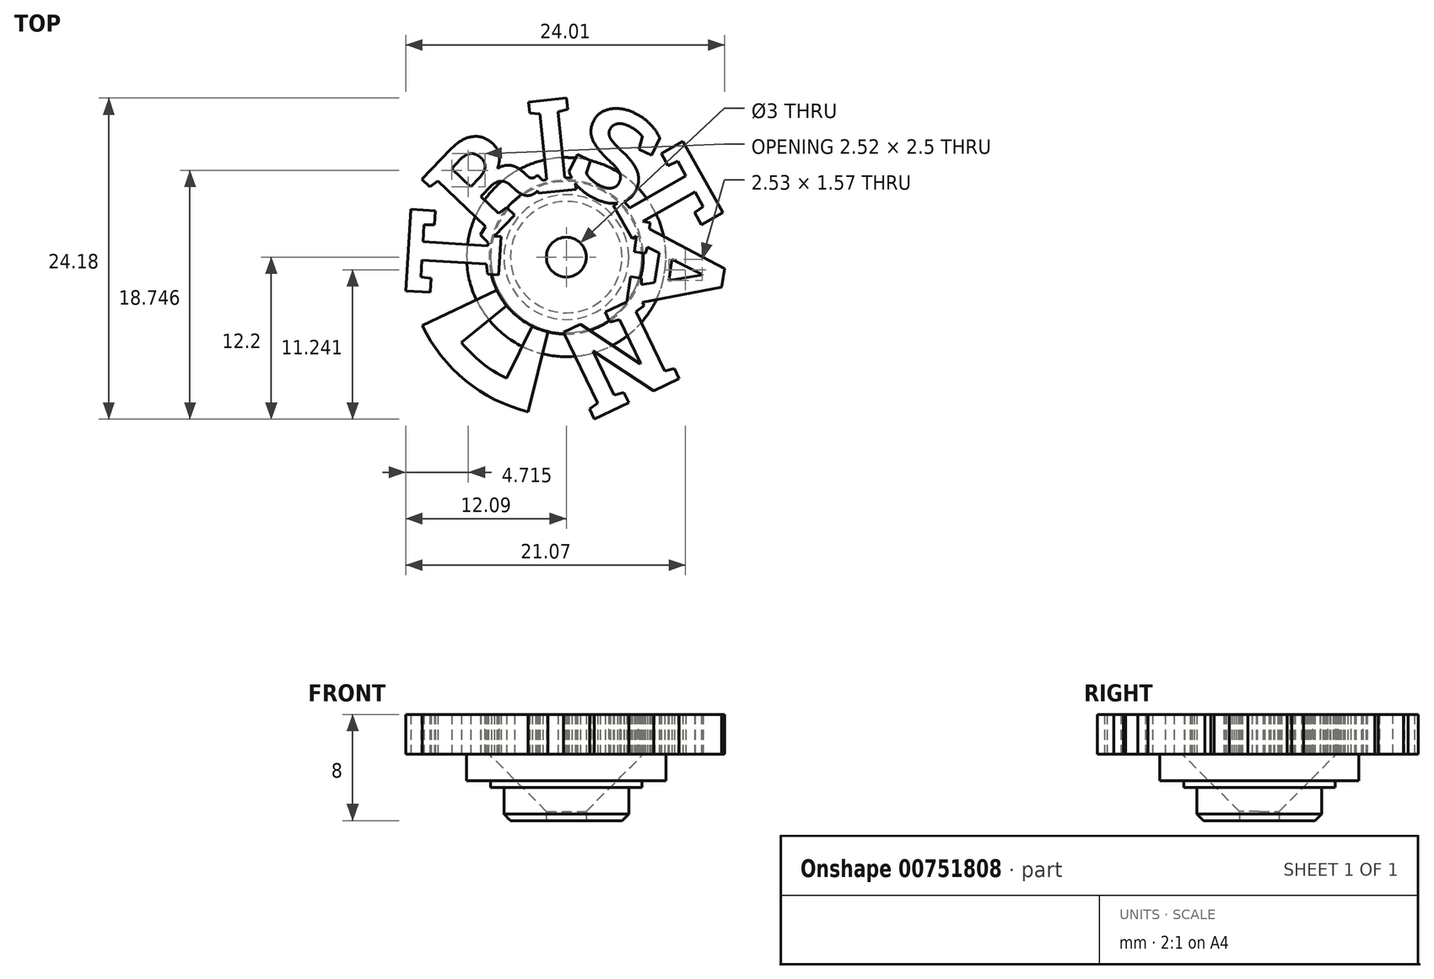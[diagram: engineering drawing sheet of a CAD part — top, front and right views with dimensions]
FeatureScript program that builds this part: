
annotation { "Feature Type Name" : "Feature", "Feature Type Description" : "" }
export const myFeature = defineFeature(function(context is Context, id is Id, definition is map)
    precondition{}
    {
        {
            var Q0;
            Q0=qCreatedBy(makeId("Top.planeOp"),FACE);
            var sketch = newSketch(context, id + "F0", { "sketchPlane" : qUnion([Q0])});
            skCircle(sketch, "E0", {"center": v(0, 0) * mm, "radius": 7.5 * mm});
            skLineSegment(sketch, "E1", {"start": v(0, 19.33) * mm, "end": v(0, -22.56) * mm, "construction": true});
            skLineSegment(sketch, "E2", {"start": v(17.52, 0) * mm, "end": v(-21.05, 0) * mm, "construction": true});
            skSolve(sketch);
        }
        {
            var Q0;
            Q0=qSketchRegion(id+"F0",true);
            extrude(context, id + "F1", {"entities" : qUnion([Q0]), "depth" : 2 * mm, "offsetDistance" : 25 * mm});
        }
        {
            var Q0;
            Q0=makeQuery(id+"F1.opExtrude","CAP_FACE",FACE,{"disambiguationData":[OSD([sQuery(id+"F0.wireOp",EDGE,"E0")])],"isStart":true});
            var sketch = newSketch(context, id + "F2", { "sketchPlane" : qUnion([Q0])});
            skCircle(sketch, "E3", {"center": v(0, 0) * mm, "radius": 4.7 * mm});
            skSolve(sketch);
        }
        {
            var Q0;
            Q0=qSketchRegion(id+"F2",true);
            extrude(context, id + "F3", {"entities" : qUnion([Q0]), "operationType" : NewBodyOperationType.ADD, "depth" : 3 * mm, "offsetDistance" : 25 * mm});
        }
        {
            var Q0;
            Q0=makeQuery(id+"F3.opExtrude","CAP_EDGE",EDGE,{"disambiguationData":[OSD([sQuery(id+"F2.wireOp",EDGE,"E3")])],"isStart":false});
            chamfer(context, id + "F4", {"entities" : qUnion([Q0]), "width" : .5 * mm, "tangentPropagation" : true});
        }
        {
            var Q0;
            Q0=makeQuery(id+"F3.opExtrude","CAP_FACE",FACE,{"disambiguationData":[OSD([sQuery(id+"F2.wireOp",EDGE,"E3")])],"isStart":false});
            var sketch = newSketch(context, id + "F5", { "sketchPlane" : qUnion([Q0])});
            skCircle(sketch, "E4", {"center": v(0, 0) * mm, "radius": 1.5 * mm});
            skSolve(sketch);
        }
        {
            var Q0;
            Q0=qSketchRegion(id+"F5",true);
            extrude(context, id + "F6", {"entities" : qUnion([Q0]), "operationType" : NewBodyOperationType.REMOVE, "oppositeDirection" : true, "depth" : 25 * mm, "offsetDistance" : 25 * mm});
        }
        {
            var Q0;
            Q0=makeQuery(id+"F1.opExtrude","CAP_FACE",FACE,{"disambiguationData":[OSD([sQuery(id+"F0.wireOp",EDGE,"E0")])],"isStart":true});
            var sketch = newSketch(context, id + "F7", { "sketchPlane" : qUnion([Q0])});
            skCircle(sketch, "E5.0", {"center": v(0, 0) * mm, "radius": 5.7 * mm});
            skCircle(sketch, "E6.0", {"center": v(0, 0) * mm, "radius": 4.7 * mm});
            skSolve(sketch);
        }
        {
            var Q0;
            Q0=qSketchRegion(id+"F7",true);
            extrude(context, id + "F8", {"entities" : qUnion([Q0]), "operationType" : NewBodyOperationType.ADD, "depth" : .5 * mm, "offsetDistance" : 25 * mm});
        }
        {
            var Q0;
            Q0=makeQuery(id+"F1.opExtrude","CAP_FACE",FACE,{"disambiguationData":[OSD([sQuery(id+"F0.wireOp",EDGE,"E0")])],"isStart":true});
            var sketch = newSketch(context, id + "F9", { "sketchPlane" : qUnion([Q0])});
            skLineSegment(sketch, "E7", {"start": v(0, 15.67) * mm, "end": v(0, -20.26) * mm, "construction": true});
            skCircle(sketch, "E8.0", {"center": v(0, 0) * mm, "radius": 7.5 * mm, "construction": true});
            skCircle(sketch, "E9", {"center": v(0, 13.5) * mm, "radius": 8 * mm});
            skSolve(sketch);
        }
        {
            var Q0;
            Q0=makeQuery(id+"F1.opExtrude","CAP_FACE",FACE,{"disambiguationData":[OSD([sQuery(id+"F0.wireOp",EDGE,"E0")])],"isStart":false});
            var sketch = newSketch(context, id + "F10", { "sketchPlane" : qUnion([Q0])});
            skText(sketch, "E10", { "text": "T", "fontName": "RobotoSlab-Bold.ttf"});
            skText(sketch, "E11", { "text": "R", "fontName": "RobotoSlab-Bold.ttf"});
            skText(sketch, "E12", { "text": "S", "fontName": "RobotoSlab-Bold.ttf"});
            skText(sketch, "E13", { "text": "I", "fontName": "RobotoSlab-Bold.ttf"});
            skLineSegment(sketch, "E14", {"start": v(0, 0) * mm, "end": v(-14.17, 0.88) * mm, "construction": true});
            skLineSegment(sketch, "E15", {"start": v(0, 0) * mm, "end": v(6.52, 13.36) * mm, "construction": true});
            skLineSegment(sketch, "E16", {"start": v(0, 0) * mm, "end": v(-1.68, 15.95) * mm, "construction": true});
            skLineSegment(sketch, "E17", {"start": v(0, 0) * mm, "end": v(-10.72, 10.25) * mm, "construction": true});
            skLineSegment(sketch, "E18", {"start": v(0, 0) * mm, "end": v(21.4, 0) * mm, "construction": true});
            skLineSegment(sketch, "E19", {"start": v(0, 0) * mm, "end": v(17.45, 9.85) * mm, "construction": true});
            skLineSegment(sketch, "E20", {"start": v(0, 0) * mm, "end": v(19.12, -2.83) * mm, "construction": true});
            skText(sketch, "E21", { "text": "T", "fontName": "RobotoSlab-Bold.ttf"});
            skText(sketch, "E22", { "text": "A", "fontName": "RobotoSlab-Bold.ttf"});
            skText(sketch, "E23", { "text": "N", "fontName": "RobotoSlab-Bold.ttf"});
            skLineSegment(sketch, "E24", {"start": v(0, 0) * mm, "end": v(0.1, -0.21) * mm, "construction": true});
            const initialGuessF10  = {"E10": [-0.0052, -0.00316, 0.06209, 0.99807, 0.007], "E11": [-0.00606, 0.0009, 0.69117, 0.7227, 0.007], "E12": [-0.0006, 0.00586, 0.8988, -0.43837, 0.007], "E13": [-0.00237, 0.00478, 0.99452, 0.10453, 0.007], "E21": [0.00265, 0.00548, 0.49155, -0.87085, 0.007], "E22": [0.00549, 0.00292, -0.14654, -0.9892, 0.007], "E23": [0.00574, -0.0028, -0.90165, -0.43247, 0.007]};
            skSetInitialGuess(sketch, initialGuessF10);
            skSolve(sketch);
        }
        {
            var Q0;
            Q0=makeQuery(id+"F6.boolean.opBoolean","INTERSECT",EDGE,{"derivedFrom":[makeQuery(id+"F1.opExtrude","CAP_FACE",FACE,{"disambiguationData":[OSD([sQuery(id+"F0.wireOp",EDGE,"E0")])],"isStart":false}),makeQuery(id+"F6.opExtrude","SWEPT_FACE",FACE,{"disambiguationData":[OSD([sQuery(id+"F5.wireOp",EDGE,"E4")])]})]});
            chamfer(context, id + "F11", {"entities" : qUnion([Q0]), "width" : 4.3 * mm, "tangentPropagation" : true});
        }
        {
            var Q0;
            Q0 = qSketchRegion(id + "F10", true);
            extrude(context, id + "F12", {"entities" : qUnion([Q0]), "operationType" : NewBodyOperationType.ADD, "depth" : 3 * mm, "offsetDistance" : 25 * mm});
        }
        {
            var Q0;
            {var subQ3=sQuery(id+"F10.wireOp",EDGE,"E10.sketch_text.stroke-8");var subQ4=sQuery(id+"F0.wireOp",EDGE,"E0");Q0=makeQuery(id+"F12.boolean.opBoolean","SPLIT",FACE,{"disambiguationData":[TD([makeQuery(id+"F12.opExtrude","SWEPT_FACE",FACE,{"disambiguationData":[OSD([subQ3])]})])],"derivedFrom":makeQuery(id+"F1.opExtrude","CAP_FACE",FACE,{"disambiguationData":[OSD([subQ4])],"isStart":false})});}
            var sketch = newSketch(context, id + "F13", { "sketchPlane" : qUnion([Q0])});
            skArc(sketch, "E25", {"start": v(-10.84, -5.15) * mm, "mid": v(-7.59, -9.3) * mm, "end": v(-2.87, -11.65) * mm});
            skArc(sketch, "E26", {"start": v(-7.9, -6.42) * mm, "mid": v(-6.36, -7.96) * mm, "end": v(-4.51, -9.13) * mm});
            skPoint(sketch, "E27.orphan", {"position": v(-5.65, -1.3) * mm});
            skPoint(sketch, "E28.orphan", {"position": v(-0.13, -5.8) * mm});
            skLineSegment(sketch, "E29.trimOffspring", {"start": v(-1.39, -5.63) * mm, "end": v(-2.87, -11.65) * mm});
            skLineSegment(sketch, "E30.trimOffspring", {"start": v(-2.57, -5.2) * mm, "end": v(-4.51, -9.13) * mm});
            skLineSegment(sketch, "E31.trimOffspring", {"start": v(-4.5, -3.66) * mm, "end": v(-7.9, -6.42) * mm});
            skLineSegment(sketch, "E32.trimOffspring", {"start": v(-5.24, -2.49) * mm, "end": v(-10.84, -5.15) * mm});
            skArc(sketch, "E33", {"start": v(-5.14, -1.32) * mm, "mid": v(-3.02, -4.36) * mm, "end": v(0.56, -5.28) * mm});
            skArc(sketch, "E34.0", {"start": v(-0.13, -5.8) * mm, "mid": v(-0.76, -5.75) * mm, "end": v(-1.39, -5.63) * mm});
            skLineSegment(sketch, "E35.0", {"start": v(-5.14, -1.32) * mm, "end": v(-5.65, -1.3) * mm});
            skLineSegment(sketch, "E36.0", {"start": v(-0.2, -5.64) * mm, "end": v(0.56, -5.28) * mm});
            skLineSegment(sketch, "E37.0", {"start": v(-0.13, -5.8) * mm, "end": v(-0.2, -5.64) * mm});
            skArc(sketch, "E38.trimOffspring", {"start": v(-2.57, -5.2) * mm, "mid": v(-3.62, -4.53) * mm, "end": v(-4.5, -3.66) * mm});
            skArc(sketch, "E39.trimOffspring", {"start": v(-5.24, -2.49) * mm, "mid": v(-5.48, -1.9) * mm, "end": v(-5.65, -1.3) * mm});
            skSolve(sketch);
        }
        {
            var Q0;
            {var subQ1=sQuery(id+"F13.wireOp",EDGE,"E25");Q0=makeQuery(id+"F13.imprint","IMPRINT",FACE,{"disambiguationData":[TD([[makeQuery(id+"F13.imprint","IMPRINT",EDGE,{"derivedFrom":subQ1}),1.0]])]});}
            var Q1;
            {var subQ0=sQuery(id+"F13.wireOp",EDGE,"E29.trimOffspring");var subQ2=sQuery(id+"F0.wireOp",EDGE,"E0");var subQ3=makeQuery(id+"F1.opExtrude","CAP_FACE",FACE,{"disambiguationData":[OSD([subQ2])],"isStart":false});var subQ6=sQuery(id+"F10.wireOp",EDGE,"E10.sketch_text.stroke-10");var subQ12=makeQuery(id+"F1.opExtrude","SWEPT_FACE",FACE,{"disambiguationData":[OSD([subQ2])]});var subQ13=makeQuery(id+"F12.boolean.opBoolean","SPLIT",EDGE,{"disambiguationData":[topologyDisambiguationEdgeConnected([subQ12,subQ3]),TD([makeQuery(id+"F12.opExtrude","SWEPT_FACE",FACE,{"disambiguationData":[OSD([subQ6])]})])],"derivedFrom":makeQuery(id+"F1.opExtrude","CAP_EDGE",EDGE,{"disambiguationData":[OSD([subQ2])],"isStart":false})});var subQ14=makeQuery(id+"F13.imprint","INTERSECT",VERTEX,{"derivedFrom":[subQ13,subQ0]});Q1=makeQuery(id+"F13.imprint","IMPRINT",FACE,{"disambiguationData":[TD([[makeQuery(id+"F13.imprint","IMPRINT",EDGE,{"disambiguationData":[TD([[subQ14,1.0]])],"derivedFrom":subQ0}),-1.0]])]});}
            var Q2;
            {var subQ0=sQuery(id+"F13.wireOp",EDGE,"E31.trimOffspring");var subQ2=sQuery(id+"F0.wireOp",EDGE,"E0");var subQ3=makeQuery(id+"F1.opExtrude","CAP_FACE",FACE,{"disambiguationData":[OSD([subQ2])],"isStart":false});var subQ6=sQuery(id+"F10.wireOp",EDGE,"E10.sketch_text.stroke-10");var subQ12=makeQuery(id+"F1.opExtrude","SWEPT_FACE",FACE,{"disambiguationData":[OSD([subQ2])]});var subQ13=makeQuery(id+"F12.boolean.opBoolean","SPLIT",EDGE,{"disambiguationData":[topologyDisambiguationEdgeConnected([subQ12,subQ3]),TD([makeQuery(id+"F12.opExtrude","SWEPT_FACE",FACE,{"disambiguationData":[OSD([subQ6])]})])],"derivedFrom":makeQuery(id+"F1.opExtrude","CAP_EDGE",EDGE,{"disambiguationData":[OSD([subQ2])],"isStart":false})});var subQ14=makeQuery(id+"F13.imprint","INTERSECT",VERTEX,{"derivedFrom":[subQ13,subQ0]});Q2=makeQuery(id+"F13.imprint","IMPRINT",FACE,{"disambiguationData":[TD([[makeQuery(id+"F13.imprint","IMPRINT",EDGE,{"disambiguationData":[TD([[subQ14,1.0]])],"derivedFrom":subQ0}),-1.0]])]});}
            extrude(context, id + "F14", {"entities" : qUnion([Q0, Q1, Q2]), "operationType" : NewBodyOperationType.ADD, "depth" : 3 * mm, "offsetDistance" : 25 * mm});
        }
    });
